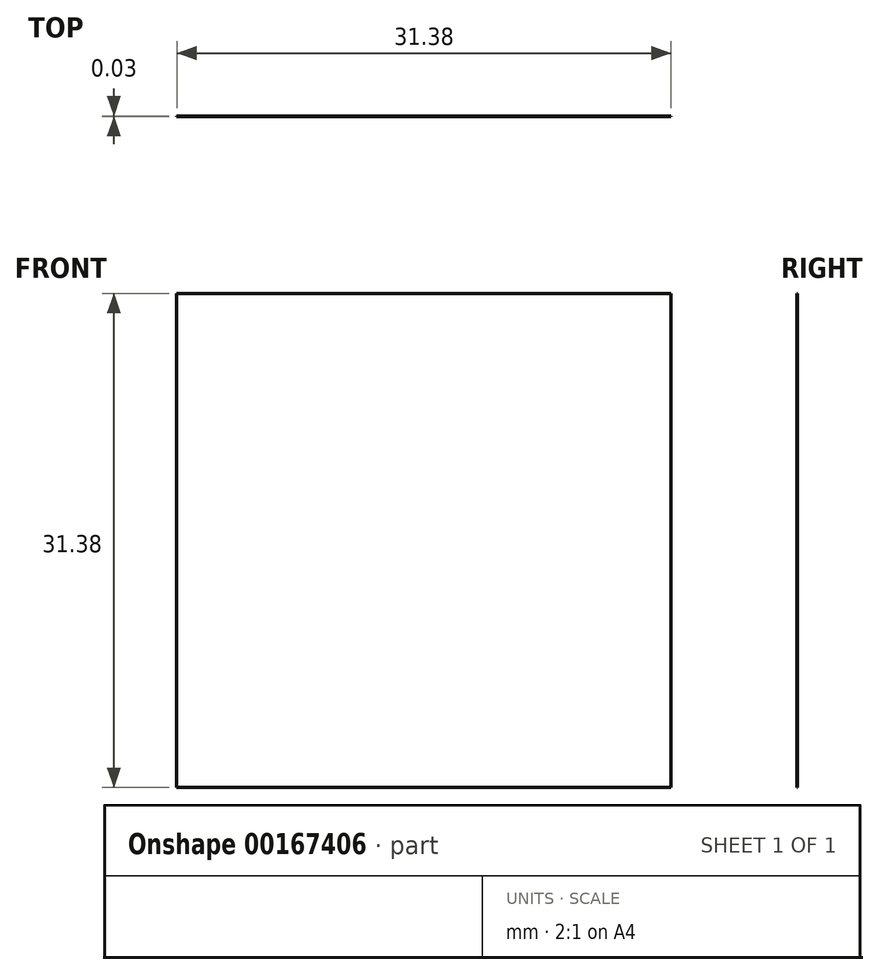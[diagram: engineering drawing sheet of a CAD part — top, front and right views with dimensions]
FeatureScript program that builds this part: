
annotation { "Feature Type Name" : "Feature", "Feature Type Description" : "" }
export const myFeature = defineFeature(function(context is Context, id is Id, definition is map)
    precondition{}
    {
        {
            var Q0;
            Q0=qCreatedBy(makeId("Front.planeOp"),FACE);
            var sketch = newSketch(context, id + "F0", { "sketchPlane" : qUnion([Q0])});
            skLineSegment(sketch, "E0.bottom", {"start": v(15.7, -15.7) * mm, "end": v(-15.7, -15.7) * mm});
            skLineSegment(sketch, "E0.top", {"start": v(15.7, 15.7) * mm, "end": v(-15.7, 15.7) * mm});
            skLineSegment(sketch, "E0.left", {"start": v(15.7, -15.7) * mm, "end": v(15.7, 15.7) * mm});
            skLineSegment(sketch, "E0.right", {"start": v(-15.7, -15.7) * mm, "end": v(-15.7, 15.7) * mm});
            skPoint(sketch, "E0.middle", {"position": v(0, 0) * mm});
            skSolve(sketch);
        }
        {
            var Q0;
            Q0=makeQuery(id+"F0.imprint","IMPRINT",FACE,{"disambiguationData":[TD([[makeQuery(id+"F0.imprint","IMPRINT",EDGE,{"derivedFrom":sQuery(id+"F0.wireOp",EDGE,"E0.bottom")}),-1.0]])]});
            extrude(context, id + "F1", {"entities" : qUnion([Q0]), "depth" : 0.03 * mm});
        }
    });
